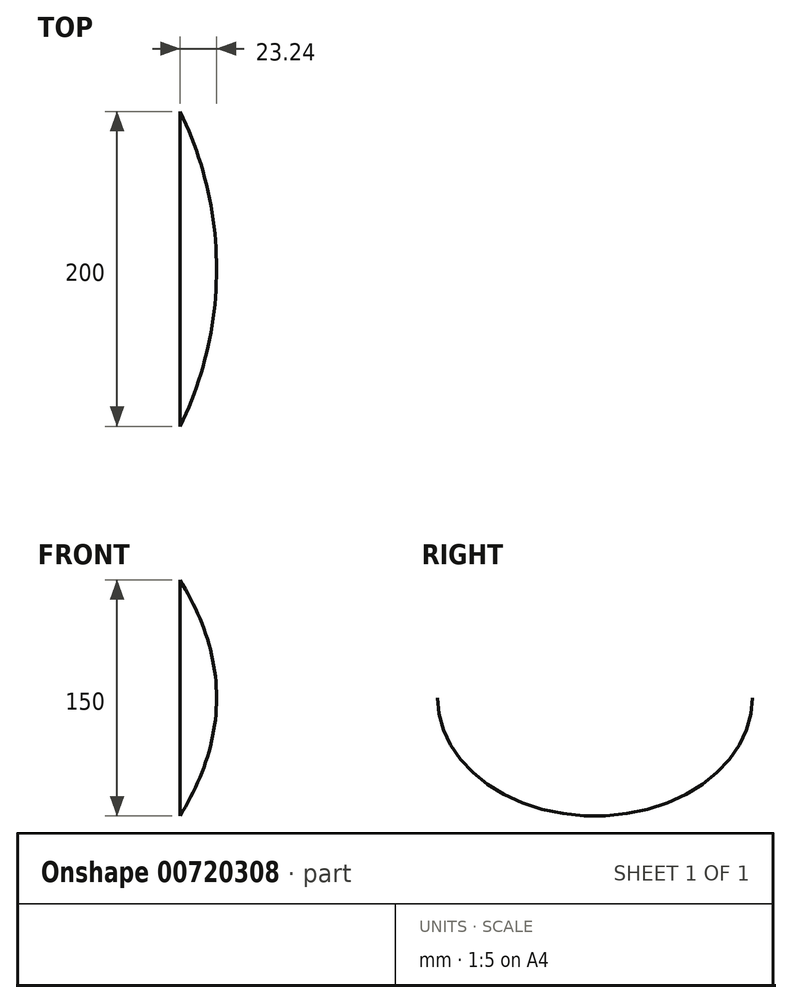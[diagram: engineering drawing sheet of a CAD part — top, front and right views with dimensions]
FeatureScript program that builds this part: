
annotation { "Feature Type Name" : "Feature", "Feature Type Description" : "" }
export const myFeature = defineFeature(function(context is Context, id is Id, definition is map)
    precondition{}
    {
        {
            var Q0;
            Q0=qCreatedBy(makeId("Right.planeOp"),FACE);
            var sketch = newSketch(context, id + "F0", { "sketchPlane" : qUnion([Q0])});
            skEllipse(sketch, "E0", {"center": v(0, 0) * mm, "majorRadius": 100 * mm, "minorRadius": 75 * mm, "majorAxis": v(1, 0)});
            skSolve(sketch);
        }
        {
            var Q0;
            Q0=qCreatedBy(makeId("Front.planeOp"),FACE);
            var sketch = newSketch(context, id + "F1", { "sketchPlane" : qUnion([Q0])});
            skArc(sketch, "E1", {"start": v(0, -75) * mm, "mid": v(23.24, 0) * mm, "end": v(0, 75) * mm});
            skSolve(sketch);
        }
        {
            var Q0;
            Q0=qCreatedBy(makeId("Top.planeOp"),FACE);
            var sketch = newSketch(context, id + "F2", { "sketchPlane" : qUnion([Q0])});
            skArc(sketch, "E2", {"start": v(0, -100) * mm, "mid": v(17.35, -51.33) * mm, "end": v(23.24, 0) * mm});
            skArc(sketch, "E3", {"start": v(23.24, 0) * mm, "mid": v(17.35, 51.33) * mm, "end": v(0, 100) * mm});
            skSolve(sketch);
        }
        {
            var Q0;
            Q0=makeQuery(id+"F0.imprint","IMPRINT",FACE,{"disambiguationData":[TD([[makeQuery(id+"F0.imprint","IMPRINT",EDGE,{"derivedFrom":sQuery(id+"F0.wireOp",EDGE,"E0")}),1.0]])]});
            var Q1;
            Q1=sQuery(id+"F2.wireOp",VERTEX,"E3.start");
            var Q2;
            Q2=sQuery(id+"F2.wireOp",EDGE,"E2");
            var Q3;
            Q3=sQuery(id+"F2.wireOp",EDGE,"E3");
            loft(context, id + "F3", {"addGuides" : true, "sheetProfilesArray" : [{ "sheetProfileEntities" : qUnion([Q0]) }, { "sheetProfileEntities" : qUnion([Q1]) }], "guidesArray" : [{ "guideEntities" : qUnion([Q2]), "guideDerivativeType" : LoftGuideDerivativeType.DEFAULT, "guideDerivativeMagnitude" : 1 }, { "guideEntities" : qUnion([Q3]), "guideDerivativeType" : LoftGuideDerivativeType.DEFAULT, "guideDerivativeMagnitude" : 1 }]});
        }
    });
